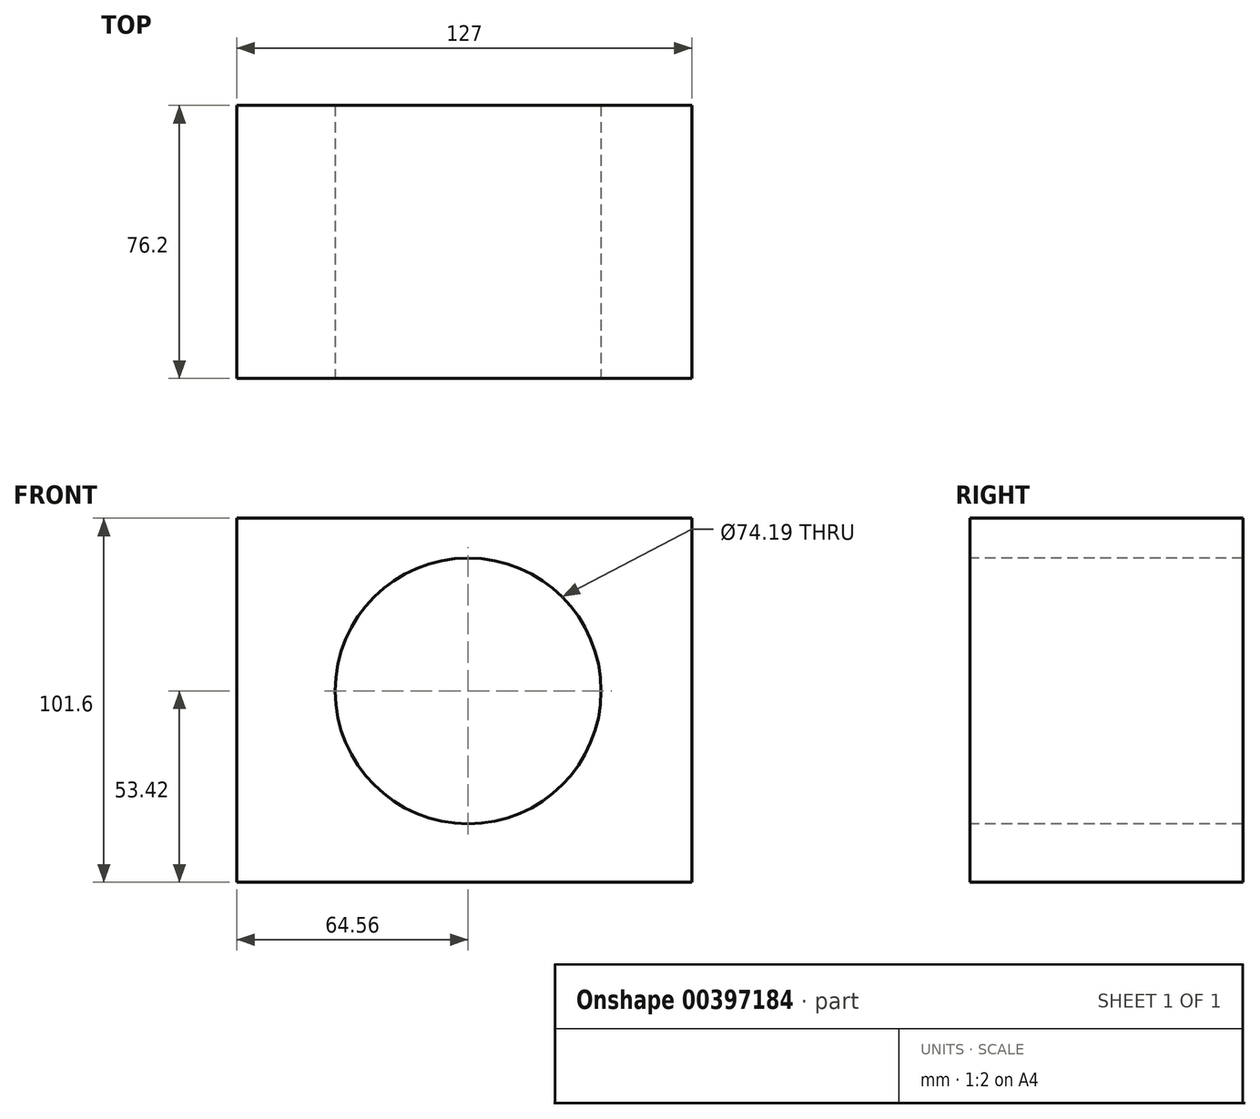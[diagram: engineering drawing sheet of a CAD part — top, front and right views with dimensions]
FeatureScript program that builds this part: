
annotation { "Feature Type Name" : "Feature", "Feature Type Description" : "" }
export const myFeature = defineFeature(function(context is Context, id is Id, definition is map)
    precondition{}
    {
        {
            var Q0;
            Q0=qCreatedBy(makeId("Front.planeOp"),FACE);
            var sketch = newSketch(context, id + "F0", { "sketchPlane" : qUnion([Q0])});
            skLineSegment(sketch, "E0.bottom", {"start": v(-64.56, 48.18) * mm, "end": v(62.44, 48.18) * mm});
            skLineSegment(sketch, "E0.top", {"start": v(-64.56, -53.42) * mm, "end": v(62.44, -53.42) * mm});
            skLineSegment(sketch, "E0.left", {"start": v(-64.56, 48.18) * mm, "end": v(-64.56, -53.42) * mm});
            skLineSegment(sketch, "E0.right", {"start": v(62.44, 48.18) * mm, "end": v(62.44, -53.42) * mm});
            skSolve(sketch);
        }
        {
            var Q0;
            Q0 = qSketchRegion(id + "F0", true);
            extrude(context, id + "F1", {"entities" : qUnion([Q0]), "endBound" : BoundingType.SYMMETRIC, "depth" : 76.2 * mm});
        }
        {
            var Q0;
            Q0=makeQuery(id+"F1.opExtrude","CAP_FACE",FACE,{"disambiguationData":[OSD([sQuery(id+"F0.wireOp",EDGE,"E0.bottom"),sQuery(id+"F0.wireOp",EDGE,"E0.top"),sQuery(id+"F0.wireOp",EDGE,"E0.left"),sQuery(id+"F0.wireOp",EDGE,"E0.right")])],"isStart":false});
            var sketch = newSketch(context, id + "F2", { "sketchPlane" : qUnion([Q0])});
            skCircle(sketch, "E1", {"center": v(0, 0) * mm, "radius": 37.1 * mm});
            skSolve(sketch);
        }
        {
            var Q0;
            Q0=makeQuery(id+"F2.imprint","IMPRINT",FACE,{"disambiguationData":[TD([[makeQuery(id+"F2.imprint","IMPRINT",EDGE,{"derivedFrom":sQuery(id+"F2.wireOp",EDGE,"E1")}),1.0]])]});
            var Q1;
            Q1=sQuery(id+"F2.wireOp",EDGE,"E1");
            extrude(context, id + "F3", {"entities" : qUnion([Q0]), "operationType" : NewBodyOperationType.REMOVE, "surfaceEntities" : qUnion([Q1]), "endBound" : BoundingType.THROUGH_ALL, "oppositeDirection" : true, "depth" : 25.4 * mm});
        }
    });
